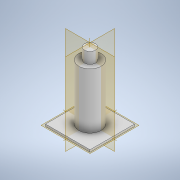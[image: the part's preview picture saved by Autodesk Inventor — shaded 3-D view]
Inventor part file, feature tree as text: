
AUTODESK INVENTOR PART (.ipt)
format: ipt  version: 2022.4 (Build 264492010, 492A)  size: 131,584 bytes
history: native  units: mm
features: extrude x4, sketch x4
ambient origin geometry x8: Origin, YZ Plane, XZ Plane, XY Plane, X Axis, Y Axis, Z Axis, Center Point
bodies: Solid1 (feature_tree)
feature tree (8):
  extrude  "Extrusion1"  Depth=20.0mm
  extrude  "Extrusion2"  Depth=5.0mm
  extrude  "Extrusion3"  Depth=5.0mm
  extrude  "Extrusion4"  Depth=2.5mm TaperAngle=0.0deg
  sketch  "Sketch1"  dims[d0=20.0mm d1=20.0mm]
  sketch  "Sketch2"  dims[d2=1.0mm d3=0.0mm d4=5.0mm]
  sketch  "Sketch3"  dims[d5=5.0mm d6=5.0mm]
  sketch  "Sketch7"  dims[d7=20.0mm d9=360.0deg d11=2.5mm d12=0.0mm d13=10.0mm d14=25.0mm d15=0.0mm d50=5.0mm d51=5.0mm d52=0.0mm]
